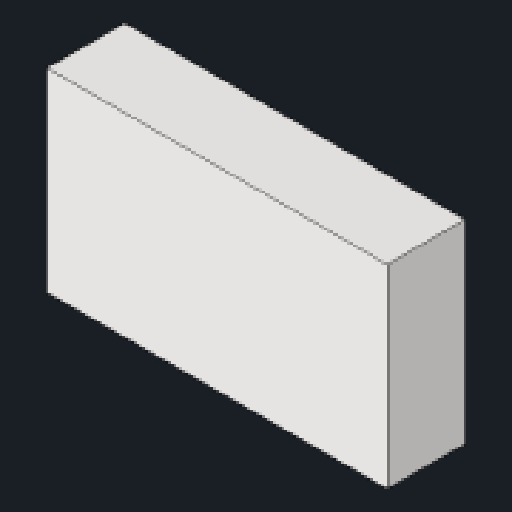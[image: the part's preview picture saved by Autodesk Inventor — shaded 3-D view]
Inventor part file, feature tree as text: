
AUTODESK INVENTOR PART (.ipt)
format: ipt  version: 2023.2 (Build 272271030, 271C)  size: 79,360 bytes
history: native  units: mm
features: extrude x1, sketch x1
ambient origin geometry x8: Origin, YZ Plane, XZ Plane, XY Plane, X Axis, Y Axis, Z Axis, Center Point
bodies: Solid1 (feature_tree)
feature tree (2):
  extrude  "Extrusion1"  Depth=20.0mm
  sketch  "Sketch1"  dims[d0=35.0mm d1=20.0mm d2=8.0mm d3=0.0mm]
